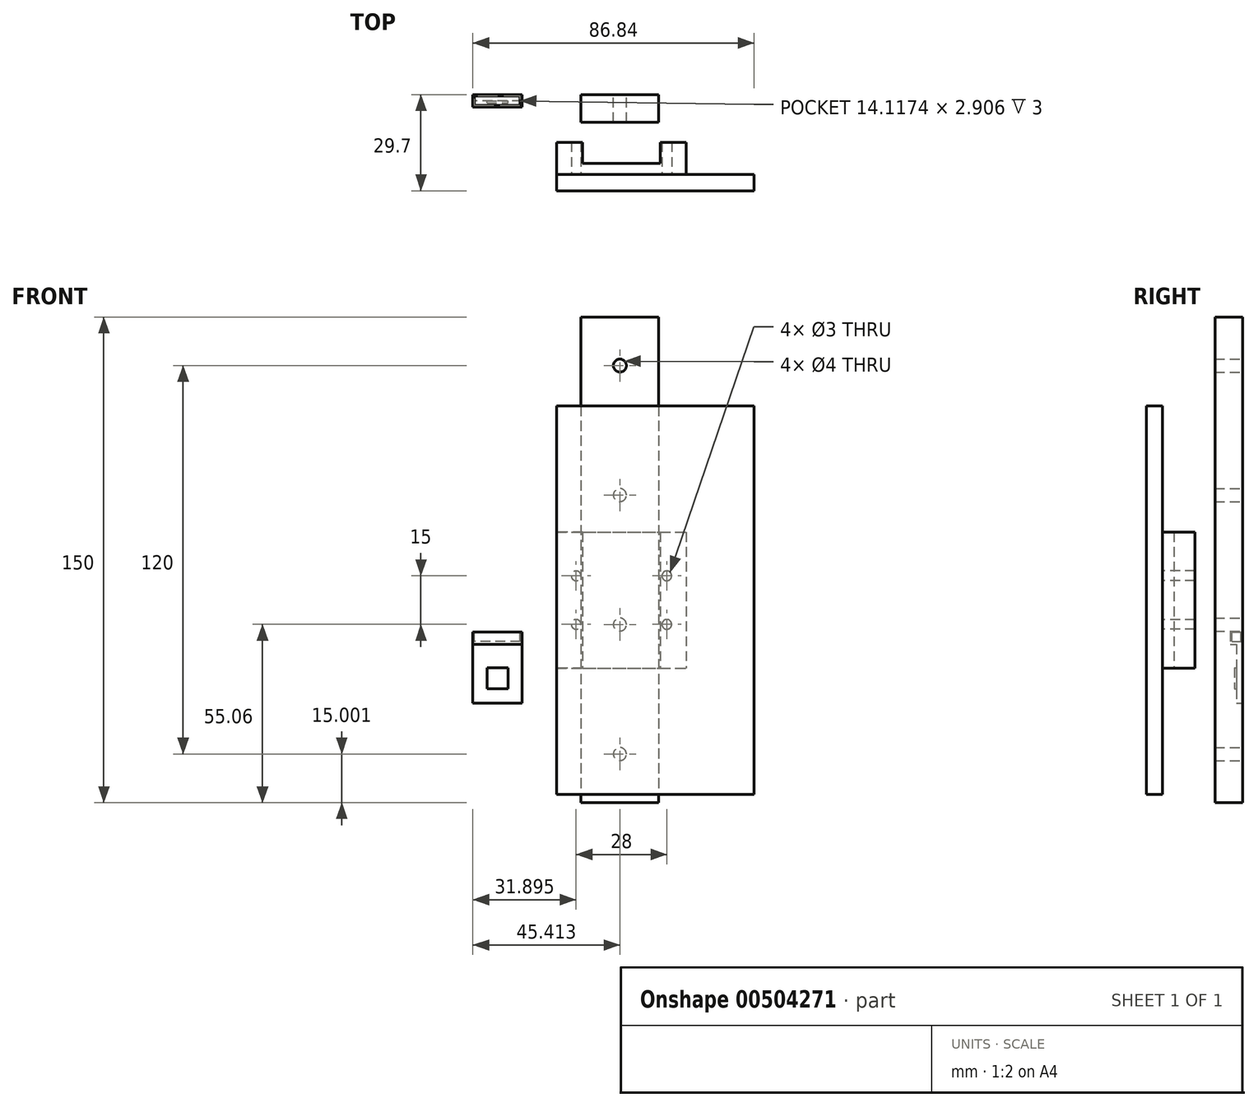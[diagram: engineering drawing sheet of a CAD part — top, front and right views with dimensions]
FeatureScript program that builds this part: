
annotation { "Feature Type Name" : "Feature", "Feature Type Description" : "" }
export const myFeature = defineFeature(function(context is Context, id is Id, definition is map)
    precondition{}
    {
        {
            var Q0;
            Q0=qCreatedBy(makeId("Front.planeOp"),FACE);
            var sketch = newSketch(context, id + "F0", { "sketchPlane" : qUnion([Q0])});
            skLineSegment(sketch, "E0.bottom", {"start": v(7.6, 11.16) * mm, "end": v(-7.6, 11.16) * mm});
            skLineSegment(sketch, "E0.top", {"start": v(7.6, -10.84) * mm, "end": v(-7.6, -10.84) * mm});
            skLineSegment(sketch, "E0.left", {"start": v(7.6, 11.16) * mm, "end": v(7.6, -10.84) * mm});
            skLineSegment(sketch, "E0.right", {"start": v(-7.6, 11.16) * mm, "end": v(-7.6, -10.84) * mm});
            skSolve(sketch);
        }
        {
            var Q0;
            Q0 = qSketchRegion(id + "F0", true);
            extrude(context, id + "F1", {"entities" : qUnion([Q0]), "depth" : 1.9 * mm});
        }
        {
            var Q0;
            Q0=makeQuery(id+"F1.opExtrude","CAP_FACE",FACE,{"disambiguationData":[OSD([sQuery(id+"F0.wireOp",EDGE,"E0.bottom"),sQuery(id+"F0.wireOp",EDGE,"E0.top"),sQuery(id+"F0.wireOp",EDGE,"E0.left"),sQuery(id+"F0.wireOp",EDGE,"E0.right")])],"isStart":false});
            var sketch = newSketch(context, id + "F2", { "sketchPlane" : qUnion([Q0])});
            skLineSegment(sketch, "E1.bottom", {"start": v(-7.6, 11.16) * mm, "end": v(7.6, 11.16) * mm});
            skLineSegment(sketch, "E1.top", {"start": v(-7.6, 7.26) * mm, "end": v(7.6, 7.26) * mm});
            skLineSegment(sketch, "E1.left", {"start": v(-7.6, 11.16) * mm, "end": v(-7.6, 7.26) * mm});
            skLineSegment(sketch, "E1.right", {"start": v(7.6, 11.16) * mm, "end": v(7.6, 7.26) * mm});
            skSolve(sketch);
        }
        {
            var Q0;
            Q0 = qSketchRegion(id + "F2", true);
            extrude(context, id + "F3", {"entities" : qUnion([Q0]), "operationType" : NewBodyOperationType.ADD, "depth" : 1.9 * mm});
        }
        {
            var Q0;
            Q0=makeQuery(id+"F1.opExtrude","CAP_FACE",FACE,{"disambiguationData":[OSD([sQuery(id+"F0.wireOp",EDGE,"E0.bottom"),sQuery(id+"F0.wireOp",EDGE,"E0.top"),sQuery(id+"F0.wireOp",EDGE,"E0.left"),sQuery(id+"F0.wireOp",EDGE,"E0.right")])],"isStart":false});
            var sketch = newSketch(context, id + "F4", { "sketchPlane" : qUnion([Q0])});
            skLineSegment(sketch, "E2.bottom", {"start": v(-3.25, 0.06) * mm, "end": v(3.25, 0.06) * mm});
            skLineSegment(sketch, "E2.top", {"start": v(-3.25, -6.44) * mm, "end": v(3.25, -6.44) * mm});
            skLineSegment(sketch, "E2.left", {"start": v(-3.25, 0.06) * mm, "end": v(-3.25, -6.44) * mm});
            skLineSegment(sketch, "E2.right", {"start": v(3.25, 0.06) * mm, "end": v(3.25, -6.44) * mm});
            skSolve(sketch);
        }
        {
            var Q0;
            Q0=makeQuery(id+"F4.imprint","IMPRINT",FACE,{"disambiguationData":[TD([[makeQuery(id+"F4.imprint","IMPRINT",EDGE,{"derivedFrom":sQuery(id+"F4.wireOp",EDGE,"E2.bottom")}),-1.0]])]});
            extrude(context, id + "F5", {"entities" : qUnion([Q0]), "operationType" : NewBodyOperationType.ADD, "depth" : .6 * mm});
        }
        {
            var Q0;
            Q0=makeQuery(id+"F3.boolean.opBoolean","MERGE",FACE,{"derivedFrom":[makeQuery(id+"F1.opExtrude","SWEPT_FACE",FACE,{"disambiguationData":[OSD([sQuery(id+"F0.wireOp",EDGE,"E0.bottom")])]}),makeQuery(id+"F3.opExtrude","SWEPT_FACE",FACE,{"disambiguationData":[OSD([sQuery(id+"F2.wireOp",EDGE,"E1.bottom")])]})]});
            var sketch = newSketch(context, id + "F6", { "sketchPlane" : qUnion([Q0])});
            skLineSegment(sketch, "E3.bottom", {"start": v(7, -3.31) * mm, "end": v(-7.12, -3.31) * mm});
            skLineSegment(sketch, "E3.top", {"start": v(7, -0.4) * mm, "end": v(-7.12, -0.4) * mm});
            skLineSegment(sketch, "E3.left", {"start": v(7, -3.31) * mm, "end": v(7, -0.4) * mm});
            skLineSegment(sketch, "E3.right", {"start": v(-7.12, -3.31) * mm, "end": v(-7.12, -0.4) * mm});
            skSolve(sketch);
        }
        {
            var Q0;
            Q0 = qSketchRegion(id + "F6", true);
            extrude(context, id + "F7", {"entities" : qUnion([Q0]), "operationType" : NewBodyOperationType.REMOVE, "oppositeDirection" : true, "depth" : 3 * mm});
        }
        {
            var Q0;
            Q0=qCreatedBy(makeId("Front.planeOp"),FACE);
            var sketch = newSketch(context, id + "F8", { "sketchPlane" : qUnion([Q0])});
            skLineSegment(sketch, "E4.bottom", {"start": v(25.81, 108.44) * mm, "end": v(49.81, 108.44) * mm});
            skLineSegment(sketch, "E4.top", {"start": v(25.81, -41.56) * mm, "end": v(49.81, -41.56) * mm});
            skLineSegment(sketch, "E4.left", {"start": v(25.81, 108.44) * mm, "end": v(25.81, -41.56) * mm});
            skLineSegment(sketch, "E4.right", {"start": v(49.81, 108.44) * mm, "end": v(49.81, -41.56) * mm});
            skLineSegment(sketch, "E5", {"start": v(37.81, 108.44) * mm, "end": v(37.81, -41.56) * mm, "construction": true});
            skCircle(sketch, "E6", {"center": v(37.81, -26.56) * mm, "radius": 2 * mm});
            skCircle(sketch, "E7", {"center": v(37.81, 13.44) * mm, "radius": 2 * mm});
            skCircle(sketch, "E8", {"center": v(37.81, 53.44) * mm, "radius": 2 * mm});
            skCircle(sketch, "E9", {"center": v(37.81, 93.44) * mm, "radius": 2 * mm});
            skSolve(sketch);
        }
        {
            var Q0;
            Q0 = qSketchRegion(id + "F8", true);
            extrude(context, id + "F9", {"entities" : qUnion([Q0]), "depth" : 8.5 * mm});
        }
        {
            var Q0;
            Q0=qCreatedBy(makeId("Top.planeOp"),FACE);
            var sketch = newSketch(context, id + "F10", { "sketchPlane" : qUnion([Q0])});
            skLineSegment(sketch, "E10", {"start": v(38.3, -21.2) * mm, "end": v(26.3, -21.2) * mm});
            skLineSegment(sketch, "E11", {"start": v(26.3, -21.2) * mm, "end": v(26.3, -14.7) * mm});
            skLineSegment(sketch, "E12", {"start": v(26.3, -14.7) * mm, "end": v(18.3, -14.7) * mm});
            skLineSegment(sketch, "E13", {"start": v(18.3, -14.7) * mm, "end": v(18.3, -24.7) * mm});
            skLineSegment(sketch, "E14", {"start": v(18.3, -24.7) * mm, "end": v(38.3, -24.7) * mm});
            skLineSegment(sketch, "E15", {"start": v(38.3, -39.17) * mm, "end": v(38.3, -14.55) * mm, "construction": true});
            skLineSegment(sketch, "E16.MirrorCS", {"start": v(50.3, -14.7) * mm, "end": v(58.3, -14.7) * mm});
            skLineSegment(sketch, "E17.MirrorCS", {"start": v(58.3, -24.7) * mm, "end": v(38.3, -24.7) * mm});
            skLineSegment(sketch, "E18.MirrorCS", {"start": v(38.3, -21.2) * mm, "end": v(50.3, -21.2) * mm});
            skLineSegment(sketch, "E19.MirrorCS", {"start": v(50.3, -21.2) * mm, "end": v(50.3, -14.7) * mm});
            skLineSegment(sketch, "E20.MirrorCS", {"start": v(58.3, -14.7) * mm, "end": v(58.3, -24.7) * mm});
            skSolve(sketch);
        }
        {
            var Q0;
            Q0 = qSketchRegion(id + "F10", true);
            extrude(context, id + "F11", {"entities" : qUnion([Q0]), "depth" : 42 * mm});
        }
        {
            var Q0;
            Q0=makeQuery(id+"F11.opExtrude","SWEPT_FACE",FACE,{"disambiguationData":[OSD([sQuery(id+"F10.wireOp",EDGE,"E14"),sQuery(id+"F10.wireOp",EDGE,"E17.MirrorCS")])]});
            var sketch = newSketch(context, id + "F12", { "sketchPlane" : qUnion([Q0])});
            skLineSegment(sketch, "E21", {"start": v(58.3, 42) * mm, "end": v(18.3, 0) * mm, "construction": true});
            skLineSegment(sketch, "E22.bottom", {"start": v(24.3, 28.5) * mm, "end": v(52.3, 28.5) * mm, "construction": true});
            skLineSegment(sketch, "E22.top", {"start": v(24.3, 13.5) * mm, "end": v(52.3, 13.5) * mm, "construction": true});
            skLineSegment(sketch, "E22.left", {"start": v(24.3, 28.5) * mm, "end": v(24.3, 13.5) * mm, "construction": true});
            skLineSegment(sketch, "E22.right", {"start": v(52.3, 28.5) * mm, "end": v(52.3, 13.5) * mm, "construction": true});
            skPoint(sketch, "E22.middle", {"position": v(38.3, 21) * mm});
            skCircle(sketch, "E23", {"center": v(24.3, 28.5) * mm, "radius": 1.5 * mm});
            skCircle(sketch, "E24", {"center": v(52.3, 28.5) * mm, "radius": 1.5 * mm});
            skCircle(sketch, "E25", {"center": v(52.3, 13.5) * mm, "radius": 1.5 * mm});
            skCircle(sketch, "E26", {"center": v(24.3, 13.5) * mm, "radius": 1.5 * mm});
            skSolve(sketch);
        }
        {
            var Q0;
            Q0 = qSketchRegion(id + "F12", true);
            extrude(context, id + "F13", {"entities" : qUnion([Q0]), "operationType" : NewBodyOperationType.REMOVE, "oppositeDirection" : true, "depth" : 25 * mm});
        }
        {
            var Q0;
            Q0=makeQuery(id+"F11.opExtrude","SWEPT_FACE",FACE,{"disambiguationData":[OSD([sQuery(id+"F10.wireOp",EDGE,"E14"),sQuery(id+"F10.wireOp",EDGE,"E17.MirrorCS")])]});
            var sketch = newSketch(context, id + "F14", { "sketchPlane" : qUnion([Q0])});
            skLineSegment(sketch, "E27.bottom", {"start": v(18.3, -39) * mm, "end": v(79.24, -39) * mm});
            skLineSegment(sketch, "E27.top", {"start": v(18.3, 81) * mm, "end": v(79.24, 81) * mm});
            skLineSegment(sketch, "E27.left", {"start": v(18.3, -39) * mm, "end": v(18.3, 81) * mm});
            skLineSegment(sketch, "E27.right", {"start": v(79.24, -39) * mm, "end": v(79.24, 81) * mm});
            skLineSegment(sketch, "E28", {"start": v(18.3, 42) * mm, "end": v(58.3, 0) * mm, "construction": true});
            skLineSegment(sketch, "E29", {"start": v(38.3, 21) * mm, "end": v(38.3, 81) * mm, "construction": true});
            skSolve(sketch);
        }
        {
            var Q0;
            Q0 = qSketchRegion(id + "F14", true);
            extrude(context, id + "F15", {"entities" : qUnion([Q0]), "depth" : 5 * mm});
        }
    });
